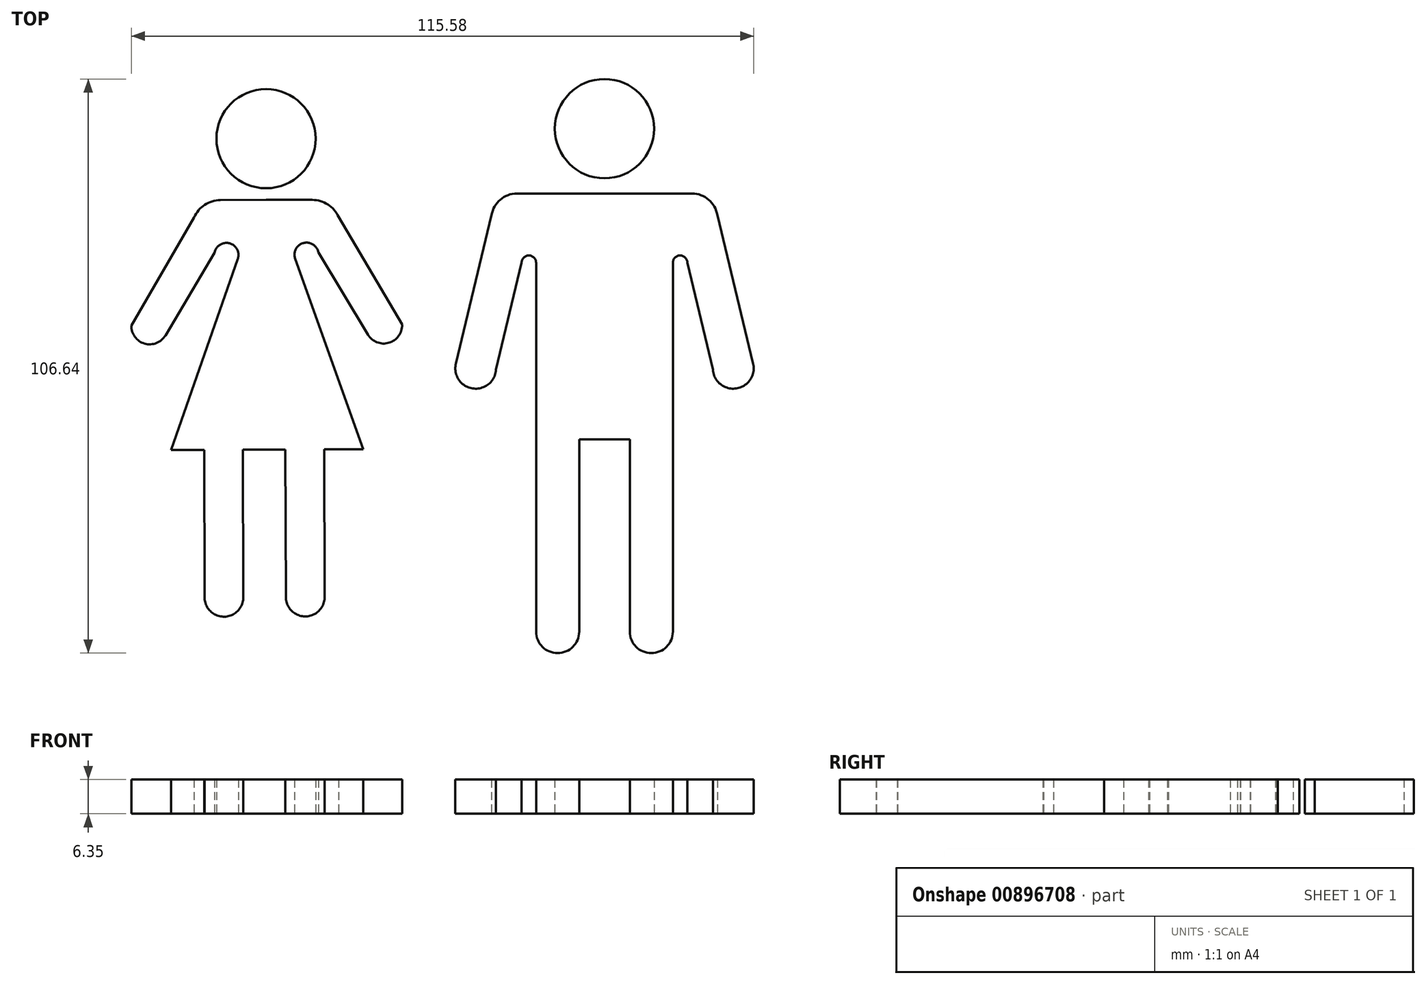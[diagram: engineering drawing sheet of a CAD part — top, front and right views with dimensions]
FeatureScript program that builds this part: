
annotation { "Feature Type Name" : "Feature", "Feature Type Description" : "" }
export const myFeature = defineFeature(function(context is Context, id is Id, definition is map)
    precondition{}
    {
        {
            var Q0;
            Q0=qCreatedBy(makeId("Top.planeOp"),FACE);
            var sketch = newSketch(context, id + "F0", { "sketchPlane" : qUnion([Q0])});
            skCircle(sketch, "E0", {"center": v(-31.74, 34.53) * mm, "radius": 9.21 * mm});
            skLineSegment(sketch, "E1", {"start": v(-31.7, 23.17) * mm, "end": v(-23.17, 23.17) * mm});
            skArc(sketch, "E2", {"start": v(-18.28, 20) * mm, "mid": v(-20.25, 22.3) * mm, "end": v(-23.17, 23.17) * mm});
            skLineSegment(sketch, "E3", {"start": v(-18.28, 20) * mm, "end": v(-6.48, 0) * mm});
            skLineSegment(sketch, "E4", {"start": v(-12.8, -1.87) * mm, "end": v(-22.02, 13.38) * mm});
            skArc(sketch, "E5", {"start": v(-12.8, -1.87) * mm, "mid": v(-8.92, -3.38) * mm, "end": v(-6.48, 0) * mm});
            skLineSegment(sketch, "E6", {"start": v(-26.33, 12.23) * mm, "end": v(-13.67, -23.17) * mm});
            skArc(sketch, "E7", {"start": v(-22.02, 13.38) * mm, "mid": v(-24.8, 15.15) * mm, "end": v(-26.33, 12.23) * mm});
            skLineSegment(sketch, "E8", {"start": v(-50.54, -23.3) * mm, "end": v(-13.67, -23.17) * mm});
            skLineSegment(sketch, "E9", {"start": v(-43.25, -23.27) * mm, "end": v(-43.15, -50.37) * mm});
            skLineSegment(sketch, "E10", {"start": v(-36.05, -23.25) * mm, "end": v(-35.96, -50.65) * mm});
            skArc(sketch, "E11", {"start": v(-43.15, -50.37) * mm, "mid": v(-39.7, -54.26) * mm, "end": v(-35.96, -50.65) * mm});
            skLineSegment(sketch, "E12.MirrorCS", {"start": v(-28.15, -23.22) * mm, "end": v(-28.06, -50.62) * mm});
            skLineSegment(sketch, "E13.MirrorCS", {"start": v(-20.96, -23.2) * mm, "end": v(-20.87, -50.3) * mm});
            skArc(sketch, "E14.MirrorCS", {"start": v(-20.87, -50.3) * mm, "mid": v(-24.3, -54.21) * mm, "end": v(-28.06, -50.62) * mm});
            skLineSegment(sketch, "E15", {"start": v(-31.74, 34.53) * mm, "end": v(-31.39, -67.22) * mm});
            skLineSegment(sketch, "E16.MirrorCS", {"start": v(-31.7, 23.17) * mm, "end": v(-40.23, 23.1) * mm});
            skArc(sketch, "E17.MirrorCS", {"start": v(-45.1, 19.9) * mm, "mid": v(-43.14, 22.23) * mm, "end": v(-40.23, 23.1) * mm});
            skPoint(sketch, "E18.orphan", {"position": v(-50.42, -2) * mm});
            skPoint(sketch, "E19.MirrorCS.end.orphan", {"position": v(-41.31, 13.32) * mm});
            skPoint(sketch, "E20.orphan", {"position": v(-36.99, 12.2) * mm});
            skPoint(sketch, "E21.MirrorCS.end.orphan", {"position": v(-49.4, -23.3) * mm});
            skPoint(sketch, "E22.MirrorCS.end.orphan", {"position": v(-56.76, -0.17) * mm});
            skLineSegment(sketch, "E23.MirrorCS", {"start": v(-36.99, 12.2) * mm, "end": v(-49.4, -23.3) * mm});
            skArc(sketch, "E24.MirrorCS", {"start": v(-41.31, 13.32) * mm, "mid": v(-38.54, 15.1) * mm, "end": v(-36.99, 12.2) * mm});
            skLineSegment(sketch, "E25.MirrorCS", {"start": v(-50.42, -2) * mm, "end": v(-41.31, 13.32) * mm});
            skLineSegment(sketch, "E26.MirrorCS", {"start": v(-45.1, 19.9) * mm, "end": v(-56.76, -0.17) * mm});
            skArc(sketch, "E27.MirrorCS", {"start": v(-50.42, -2) * mm, "mid": v(-54.3, -3.54) * mm, "end": v(-56.76, -0.17) * mm});
            skSolve(sketch);
        }
        {
            var Q0;
            Q0=qCreatedBy(makeId("Top.planeOp"),FACE);
            var sketch = newSketch(context, id + "F1", { "sketchPlane" : qUnion([Q0])});
            skCircle(sketch, "E28", {"center": v(31.11, 36.4) * mm, "radius": 9.21 * mm});
            skLineSegment(sketch, "E29", {"start": v(14.85, 24.34) * mm, "end": v(47.38, 24.34) * mm});
            skArc(sketch, "E30", {"start": v(52.09, 20.34) * mm, "mid": v(50.47, 23.2) * mm, "end": v(47.38, 24.34) * mm});
            skLineSegment(sketch, "E31", {"start": v(52.09, 20.34) * mm, "end": v(58.72, -7.23) * mm});
            skArc(sketch, "E32", {"start": v(51.25, -8.35) * mm, "mid": v(55.6, -11.86) * mm, "end": v(58.72, -7.23) * mm});
            skLineSegment(sketch, "E33", {"start": v(51.25, -8.35) * mm, "end": v(46.5, 11.5) * mm});
            skLineSegment(sketch, "E34", {"start": v(31.11, 54.55) * mm, "end": v(31.11, -62.84) * mm});
            skPoint(sketch, "E34.startSnap0", {"position": v(31.11, 24.34) * mm});
            skArc(sketch, "E35.MirrorCS", {"start": v(10.14, 20.34) * mm, "mid": v(11.76, 23.2) * mm, "end": v(14.85, 24.34) * mm});
            skLineSegment(sketch, "E36.MirrorCS", {"start": v(10.14, 20.34) * mm, "end": v(3.51, -7.23) * mm});
            skArc(sketch, "E37.MirrorCS", {"start": v(10.98, -8.35) * mm, "mid": v(6.64, -11.86) * mm, "end": v(3.51, -7.23) * mm});
            skLineSegment(sketch, "E38.MirrorCS", {"start": v(10.98, -8.35) * mm, "end": v(15.72, 11.5) * mm});
            skLineSegment(sketch, "E39", {"start": v(18.41, 11.5) * mm, "end": v(18.41, -57.03) * mm});
            skLineSegment(sketch, "E40.MirrorCS", {"start": v(43.81, 11.5) * mm, "end": v(43.81, -57.03) * mm});
            skArc(sketch, "E41", {"start": v(46.5, 11.5) * mm, "mid": v(45.16, 12.84) * mm, "end": v(43.81, 11.5) * mm});
            skArc(sketch, "E42.MirrorCS", {"start": v(15.72, 11.5) * mm, "mid": v(17.07, 12.84) * mm, "end": v(18.41, 11.5) * mm});
            skLineSegment(sketch, "E43", {"start": v(35.81, -57.03) * mm, "end": v(35.81, -21.32) * mm});
            skLineSegment(sketch, "E44", {"start": v(35.81, -21.32) * mm, "end": v(31.11, -21.32) * mm});
            skLineSegment(sketch, "E45.MirrorCS", {"start": v(26.42, -21.32) * mm, "end": v(31.11, -21.32) * mm});
            skLineSegment(sketch, "E46.MirrorCS", {"start": v(26.42, -57.03) * mm, "end": v(26.42, -21.32) * mm});
            skArc(sketch, "E47", {"start": v(35.81, -57.03) * mm, "mid": v(39.81, -61.03) * mm, "end": v(43.81, -57.03) * mm});
            skArc(sketch, "E48.MirrorCS", {"start": v(26.42, -57.03) * mm, "mid": v(22.41, -61.03) * mm, "end": v(18.41, -57.03) * mm});
            skSolve(sketch);
        }
        {
            var Q0;
            Q0 = qSketchRegion(id + "F1", true);
            extrude(context, id + "F2", {"entities" : qUnion([Q0]), "depth" : 6.35 * mm, "offsetDistance" : 25.4 * mm});
        }
        {
            var Q0;
            Q0 = qSketchRegion(id + "F0", true);
            extrude(context, id + "F3", {"entities" : qUnion([Q0]), "depth" : 6.35 * mm, "offsetDistance" : 25.4 * mm});
        }
    });
